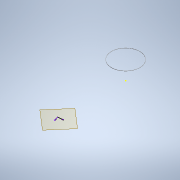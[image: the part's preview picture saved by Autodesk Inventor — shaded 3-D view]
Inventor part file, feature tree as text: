
AUTODESK INVENTOR PART (.ipt)
format: ipt  version: 2020 (Build 240168000, 168)  size: 115,200 bytes
history: native  units: mm
features: other x4, sketch x3, plane x3, reference x3, extrude x1, sweep x1
ambient origin geometry x8: Origin, YZ Plane, XZ Plane, XY Plane, X Axis, Y Axis, Z Axis, Center Point
bodies: 实体1 (feature_tree)
feature tree (15):
  sketch  "草图1"  dims[d0=10.0mm d1=0.0mm d2=0.0mm d3=0.0mm]
  plane  "工作平面1"
  extrude  "拉伸1"  TaperAngle=0.0deg  [1 undecoded]
  plane  "工作平面2"
  sketch  "草图2"
  plane  "工作平面3"
  sweep  "扫掠1"
  reference  "参考1"
  reference  "参考2"
  sketch  "草图4"
  reference  "参考3"
  other  "<userpath>\Desktop\装配3\Workspace\cpz assemble.iam"
  other  "cpz assemble.iam"
  other  "轴承通盖:1"
  other  "螺栓 GB 32.1 M6 x 30:2"
note: 1 required parameter value undecoded (feature->parameter linkage not recoverable at this tier; creation-order binding heuristic only, values carry confidence <= 0.55)
